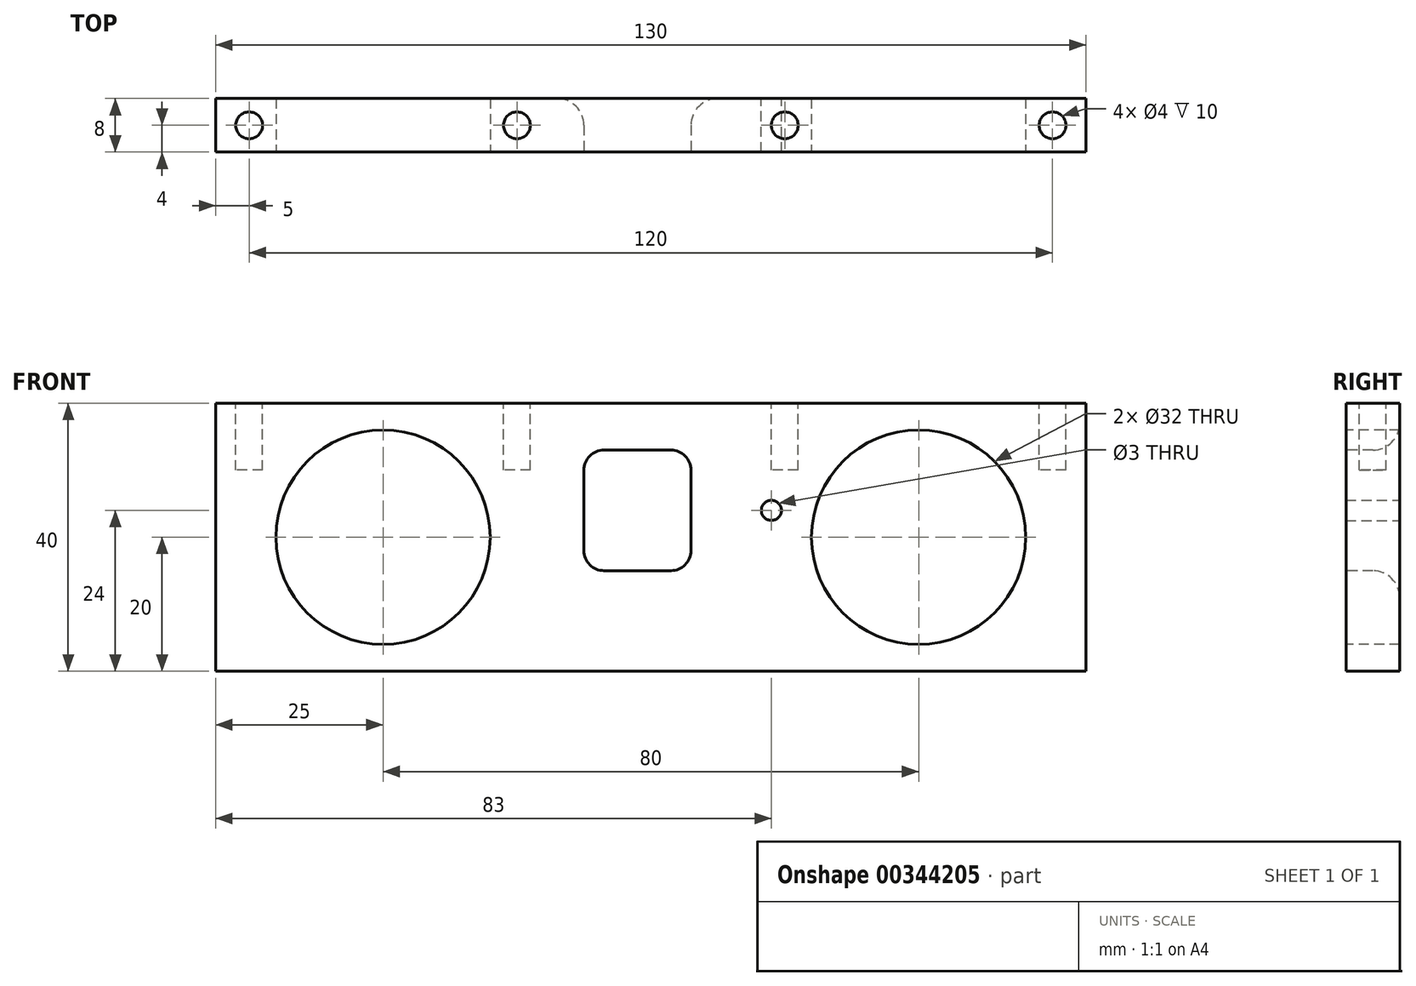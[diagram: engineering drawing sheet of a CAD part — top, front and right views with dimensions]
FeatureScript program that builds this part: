
annotation { "Feature Type Name" : "Feature", "Feature Type Description" : "" }
export const myFeature = defineFeature(function(context is Context, id is Id, definition is map)
    precondition{}
    {
        {
            var Q0;
            Q0=qCreatedBy(makeId("Front.planeOp"),FACE);
            var sketch = newSketch(context, id + "F0", { "sketchPlane" : qUnion([Q0])});
            skLineSegment(sketch, "E0.bottom", {"start": v(-65, 20) * mm, "end": v(65, 20) * mm});
            skLineSegment(sketch, "E0.top", {"start": v(-65, -20) * mm, "end": v(65, -20) * mm});
            skLineSegment(sketch, "E0.left", {"start": v(-65, 20) * mm, "end": v(-65, -20) * mm});
            skLineSegment(sketch, "E0.right", {"start": v(65, 20) * mm, "end": v(65, -20) * mm});
            skSolve(sketch);
        }
        {
            var Q0;
            Q0 = qSketchRegion(id + "F0", true);
            extrude(context, id + "F1", {"entities" : qUnion([Q0]), "depth" : 8 * mm});
        }
        {
            var Q0;
            Q0=makeQuery(id+"F1.opExtrude","CAP_FACE",FACE,{"disambiguationData":[OSD([sQuery(id+"F0.wireOp",EDGE,"E0.bottom"),sQuery(id+"F0.wireOp",EDGE,"E0.top"),sQuery(id+"F0.wireOp",EDGE,"E0.left"),sQuery(id+"F0.wireOp",EDGE,"E0.right")])],"isStart":false});
            var sketch = newSketch(context, id + "F2", { "sketchPlane" : qUnion([Q0])});
            skCircle(sketch, "E1", {"center": v(40, 0) * mm, "radius": 16 * mm});
            skCircle(sketch, "E2", {"center": v(-40, 0) * mm, "radius": 16 * mm});
            skSolve(sketch);
        }
        {
            var Q0;
            Q0 = qSketchRegion(id + "F2", true);
            extrude(context, id + "F3", {"entities" : qUnion([Q0]), "operationType" : NewBodyOperationType.REMOVE, "endBound" : BoundingType.THROUGH_ALL, "oppositeDirection" : true, "depth" : 25 * mm});
        }
        {
            var Q0;
            Q0=makeQuery(id+"F1.opExtrude","SWEPT_FACE",FACE,{"disambiguationData":[OSD([sQuery(id+"F0.wireOp",EDGE,"E0.bottom")])]});
            var sketch = newSketch(context, id + "F4", { "sketchPlane" : qUnion([Q0])});
            skCircle(sketch, "E3", {"center": v(-60, -4) * mm, "radius": 2 * mm});
            skCircle(sketch, "E4", {"center": v(60, -4) * mm, "radius": 2 * mm});
            skCircle(sketch, "E5", {"center": v(-20, -4) * mm, "radius": 2 * mm});
            skCircle(sketch, "E6", {"center": v(20, -4) * mm, "radius": 2 * mm});
            skPoint(sketch, "E7.center.orphan", {"position": v(0, -4) * mm});
            skSolve(sketch);
        }
        {
            var Q0;
            Q0 = qSketchRegion(id + "F4", true);
            extrude(context, id + "F5", {"entities" : qUnion([Q0]), "operationType" : NewBodyOperationType.REMOVE, "oppositeDirection" : true, "depth" : 10 * mm});
        }
        {
            var Q0;
            Q0=makeQuery(id+"F1.opExtrude","CAP_FACE",FACE,{"disambiguationData":[OSD([sQuery(id+"F0.wireOp",EDGE,"E0.bottom"),sQuery(id+"F0.wireOp",EDGE,"E0.top"),sQuery(id+"F0.wireOp",EDGE,"E0.left"),sQuery(id+"F0.wireOp",EDGE,"E0.right")])],"isStart":false});
            var sketch = newSketch(context, id + "F6", { "sketchPlane" : qUnion([Q0])});
            skLineSegment(sketch, "E8.bottom", {"start": v(-7, 13) * mm, "end": v(3, 13) * mm});
            skLineSegment(sketch, "E8.top", {"start": v(-7, -5) * mm, "end": v(3, -5) * mm});
            skLineSegment(sketch, "E8.left", {"start": v(-10, 10) * mm, "end": v(-10, -2) * mm});
            skLineSegment(sketch, "E8.right", {"start": v(6, 10) * mm, "end": v(6, -2) * mm});
            skPoint(sketch, "E9.visualSharp", {"position": v(-10, 13) * mm});
            skArc(sketch, "E9.filletArc", {"start": v(-7, 13) * mm, "mid": v(-9.12, 12.12) * mm, "end": v(-10, 10) * mm});
            skPoint(sketch, "E10.visualSharp", {"position": v(-10, -5) * mm});
            skArc(sketch, "E10.filletArc", {"start": v(-10, -2) * mm, "mid": v(-9.12, -4.12) * mm, "end": v(-7, -5) * mm});
            skPoint(sketch, "E11.visualSharp", {"position": v(6, 13) * mm});
            skArc(sketch, "E11.filletArc", {"start": v(6, 10) * mm, "mid": v(5.12, 12.12) * mm, "end": v(3, 13) * mm});
            skPoint(sketch, "E12.visualSharp", {"position": v(6, -5) * mm});
            skArc(sketch, "E12.filletArc", {"start": v(3, -5) * mm, "mid": v(5.12, -4.12) * mm, "end": v(6, -2) * mm});
            skSolve(sketch);
        }
        {
            var Q0;
            Q0 = qSketchRegion(id + "F6", true);
            extrude(context, id + "F7", {"entities" : qUnion([Q0]), "operationType" : NewBodyOperationType.REMOVE, "oppositeDirection" : true, "depth" : 25 * mm});
        }
        {
            var Q0;
            Q0=makeQuery(id+"F7.boolean.opBoolean","COPY",EDGE,{"derivedFrom":makeQuery(id+"F7.opExtrude","CAP_EDGE",EDGE,{"disambiguationData":[OSD([sQuery(id+"F6.wireOp",EDGE,"E8.right")])],"isStart":true})});
            var Q1;
            Q1=makeQuery(id+"F7.boolean.opBoolean","INTERSECT",EDGE,{"derivedFrom":[makeQuery(id+"F1.opExtrude","CAP_FACE",FACE,{"disambiguationData":[OSD([sQuery(id+"F0.wireOp",EDGE,"E0.bottom"),sQuery(id+"F0.wireOp",EDGE,"E0.top"),sQuery(id+"F0.wireOp",EDGE,"E0.left"),sQuery(id+"F0.wireOp",EDGE,"E0.right")])],"isStart":true}),makeQuery(id+"F7.opExtrude","SWEPT_FACE",FACE,{"disambiguationData":[OSD([sQuery(id+"F6.wireOp",EDGE,"E8.right")])]})]});
            fillet(context, id + "F8", {"entities" : qUnion([Q0, Q1]), "radius" : 4 * mm, "tangentPropagation" : true, "allowEdgeOverflow" : false});
        }
        {
            var Q0;
            Q0=makeQuery(id+"F1.opExtrude","CAP_FACE",FACE,{"disambiguationData":[OSD([sQuery(id+"F0.wireOp",EDGE,"E0.bottom"),sQuery(id+"F0.wireOp",EDGE,"E0.top"),sQuery(id+"F0.wireOp",EDGE,"E0.left"),sQuery(id+"F0.wireOp",EDGE,"E0.right")])],"isStart":true});
            var sketch = newSketch(context, id + "F9", { "sketchPlane" : qUnion([Q0])});
            skLineSegment(sketch, "E13", {"start": v(-10, 4) * mm, "end": v(-29.24, 4) * mm, "construction": true});
            skCircle(sketch, "E14", {"center": v(-18, 4) * mm, "radius": 1.5 * mm});
            skSolve(sketch);
        }
        {
            var Q0;
            Q0 = qSketchRegion(id + "F9", true);
            extrude(context, id + "F10", {"entities" : qUnion([Q0]), "operationType" : NewBodyOperationType.REMOVE, "oppositeDirection" : true, "depth" : 25 * mm});
        }
    });
